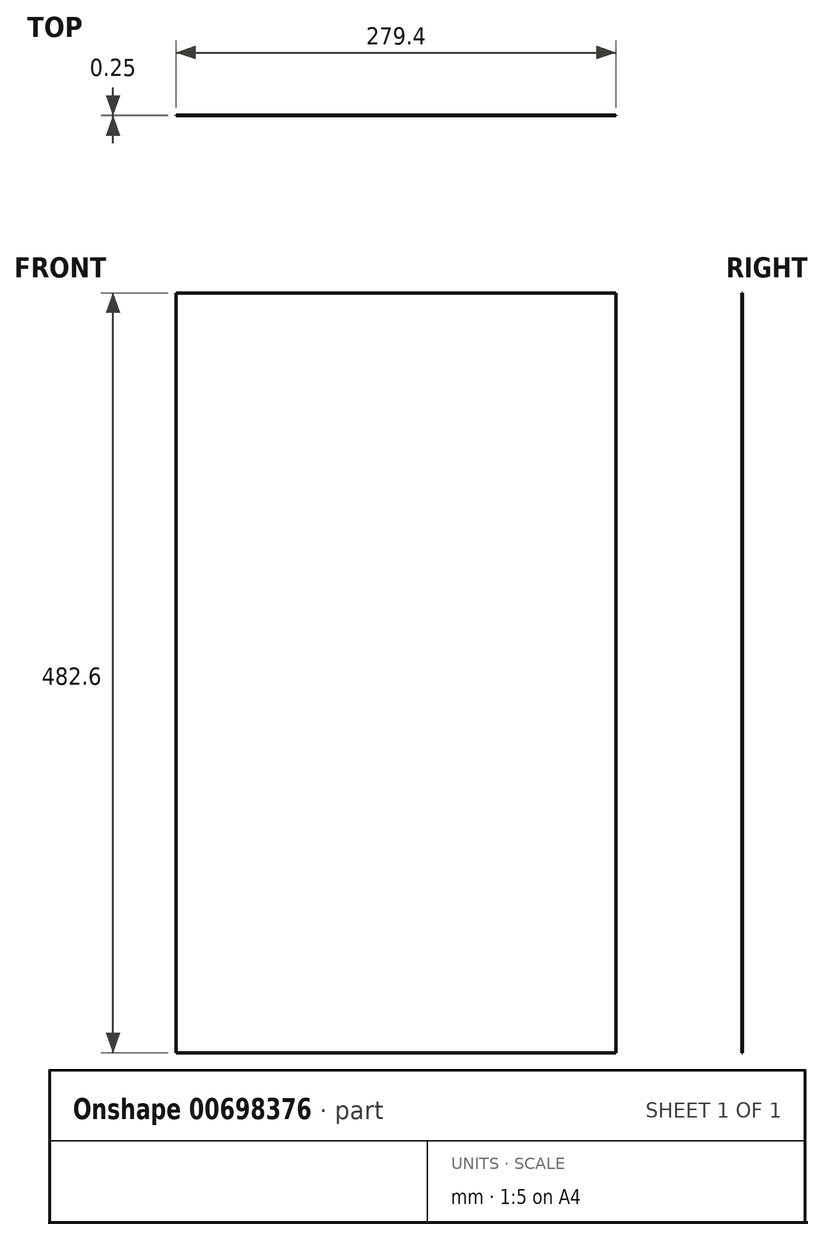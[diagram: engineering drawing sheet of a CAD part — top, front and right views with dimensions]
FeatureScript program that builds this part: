
annotation { "Feature Type Name" : "Feature", "Feature Type Description" : "" }
export const myFeature = defineFeature(function(context is Context, id is Id, definition is map)
    precondition{}
    {
        {
            var Q0;
            Q0=qCreatedBy(makeId("Front.planeOp"),FACE);
            var sketch = newSketch(context, id + "F0", { "sketchPlane" : qUnion([Q0])});
            skLineSegment(sketch, "E0.bottom", {"start": v(139.7, 241.3) * mm, "end": v(-139.7, 241.3) * mm});
            skLineSegment(sketch, "E0.top", {"start": v(139.7, -241.3) * mm, "end": v(-139.7, -241.3) * mm});
            skLineSegment(sketch, "E0.left", {"start": v(139.7, 241.3) * mm, "end": v(139.7, -241.3) * mm});
            skLineSegment(sketch, "E0.right", {"start": v(-139.7, 241.3) * mm, "end": v(-139.7, -241.3) * mm});
            skPoint(sketch, "E0.middle", {"position": v(0, 0) * mm});
            skSolve(sketch);
        }
        {
            var Q0;
            Q0=makeQuery(id+"F0.imprint","IMPRINT",FACE,{"disambiguationData":[TD([[makeQuery(id+"F0.imprint","IMPRINT",EDGE,{"derivedFrom":sQuery(id+"F0.wireOp",EDGE,"E0.bottom")}),1.0]])]});
            extrude(context, id + "F1", {"entities" : qUnion([Q0]), "depth" : 0.25 * mm, "offsetDistance" : 25.4 * mm});
        }
    });
